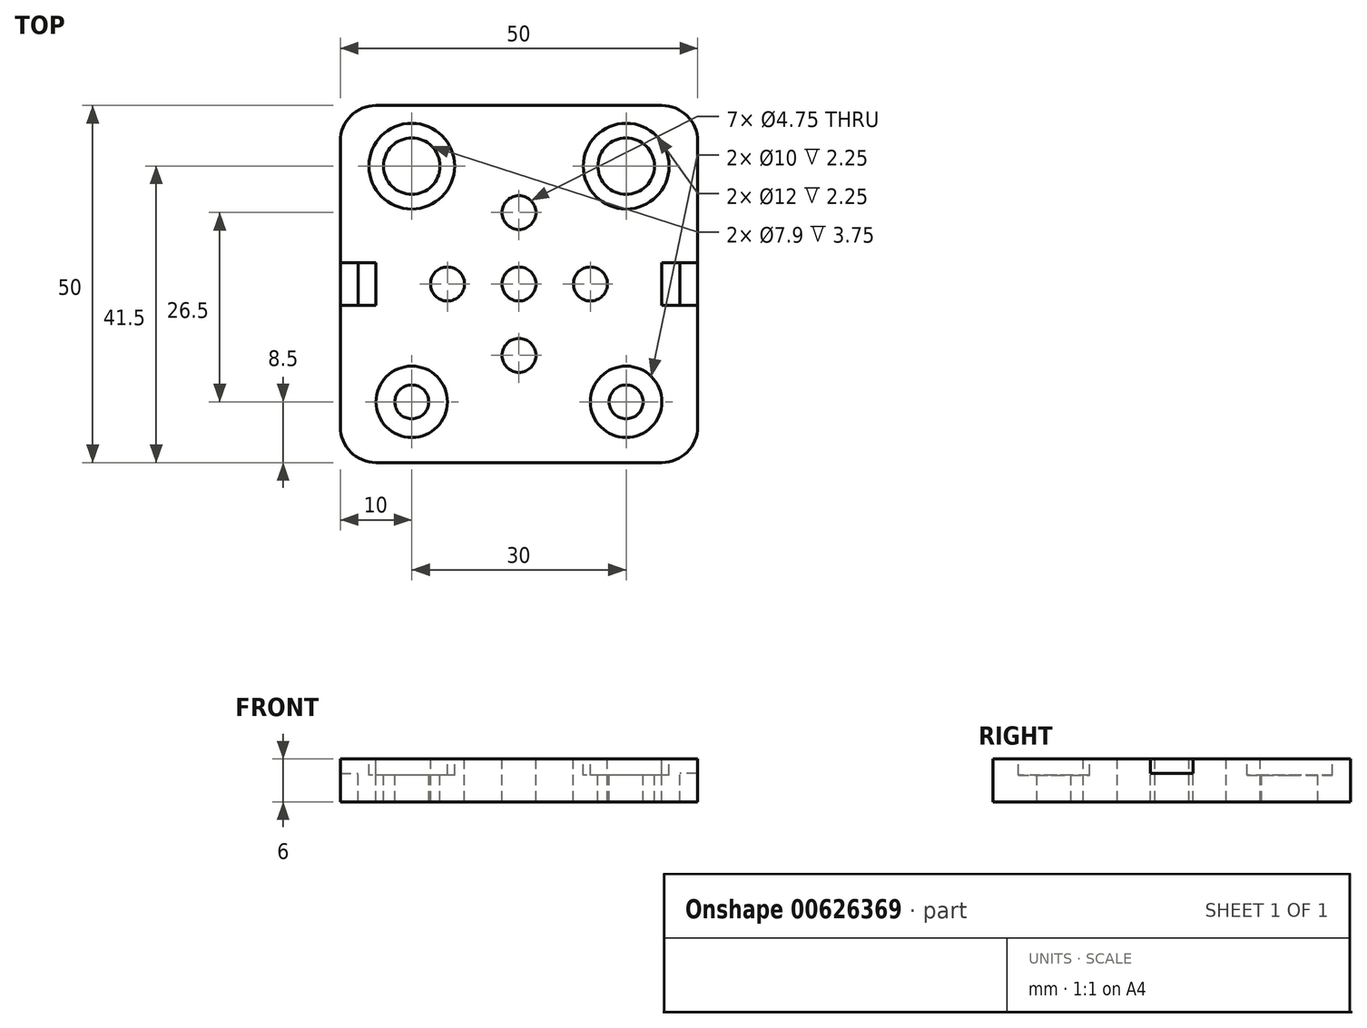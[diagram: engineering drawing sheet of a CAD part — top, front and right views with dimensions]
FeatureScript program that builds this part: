
annotation { "Feature Type Name" : "Feature", "Feature Type Description" : "" }
export const myFeature = defineFeature(function(context is Context, id is Id, definition is map)
    precondition{}
    {
        {
            var Q0;
            Q0=qCreatedBy(makeId("Top.planeOp"),FACE);
            var sketch = newSketch(context, id + "F0", { "sketchPlane" : qUnion([Q0])});
            skLineSegment(sketch, "E0.bottom", {"start": v(-20, -25) * mm, "end": v(20, -25) * mm});
            skLineSegment(sketch, "E0.top", {"start": v(-20, 25) * mm, "end": v(20, 25) * mm});
            skLineSegment(sketch, "E0.left", {"start": v(-25, -20) * mm, "end": v(-25, 20) * mm});
            skLineSegment(sketch, "E0.right", {"start": v(25, -20) * mm, "end": v(25, 20) * mm});
            skPoint(sketch, "E0.middle", {"position": v(0, 0) * mm});
            skPoint(sketch, "E1.visualSharp", {"position": v(-25, 25) * mm});
            skArc(sketch, "E1.filletArc", {"start": v(-20, 25) * mm, "mid": v(-23.54, 23.54) * mm, "end": v(-25, 20) * mm});
            skPoint(sketch, "E2.visualSharp", {"position": v(25, 25) * mm});
            skArc(sketch, "E2.filletArc", {"start": v(25, 20) * mm, "mid": v(23.54, 23.54) * mm, "end": v(20, 25) * mm});
            skPoint(sketch, "E3.visualSharp", {"position": v(25, -25) * mm});
            skArc(sketch, "E3.filletArc", {"start": v(20, -25) * mm, "mid": v(23.54, -23.54) * mm, "end": v(25, -20) * mm});
            skPoint(sketch, "E4.visualSharp", {"position": v(-25, -25) * mm});
            skArc(sketch, "E4.filletArc", {"start": v(-25, -20) * mm, "mid": v(-23.54, -23.54) * mm, "end": v(-20, -25) * mm});
            skSolve(sketch);
        }
        {
            var Q0;
            Q0=makeQuery(id+"F0.imprint","IMPRINT",FACE,{"disambiguationData":[TD([[makeQuery(id+"F0.imprint","IMPRINT",EDGE,{"derivedFrom":sQuery(id+"F0.wireOp",EDGE,"E0.bottom")}),1.0]])]});
            extrude(context, id + "F1", {"entities" : qUnion([Q0]), "depth" : 6 * mm, "offsetDistance" : 25 * mm});
        }
        {
            var Q0;
            Q0=makeQuery(id+"F1.opExtrude","CAP_FACE",FACE,{"disambiguationData":[OSD([sQuery(id+"F0.wireOp",EDGE,"E0.bottom"),sQuery(id+"F0.wireOp",EDGE,"E0.top"),sQuery(id+"F0.wireOp",EDGE,"E0.left"),sQuery(id+"F0.wireOp",EDGE,"E0.right"),sQuery(id+"F0.wireOp",EDGE,"E1.filletArc"),sQuery(id+"F0.wireOp",EDGE,"E2.filletArc"),sQuery(id+"F0.wireOp",EDGE,"E3.filletArc"),sQuery(id+"F0.wireOp",EDGE,"E4.filletArc")])],"isStart":false});
            var sketch = newSketch(context, id + "F2", { "sketchPlane" : qUnion([Q0])});
            skLineSegment(sketch, "E5.bottom", {"start": v(-25, 3) * mm, "end": v(-22.5, 3) * mm});
            skLineSegment(sketch, "E5.top", {"start": v(-25, -3) * mm, "end": v(-22.5, -3) * mm});
            skLineSegment(sketch, "E5.left", {"start": v(-25, 3) * mm, "end": v(-25, -3) * mm});
            skLineSegment(sketch, "E5.right", {"start": v(-22.5, 3) * mm, "end": v(-22.5, -3) * mm});
            skLineSegment(sketch, "E6.MirrorCS", {"start": v(25, 3) * mm, "end": v(22.5, 3) * mm});
            skLineSegment(sketch, "E7.MirrorCS", {"start": v(25, -3) * mm, "end": v(22.5, -3) * mm});
            skLineSegment(sketch, "E8.MirrorCS", {"start": v(25, 3) * mm, "end": v(25, -3) * mm});
            skLineSegment(sketch, "E9.MirrorCS", {"start": v(22.5, 3) * mm, "end": v(22.5, -3) * mm});
            skSolve(sketch);
        }
        {
            var Q0;
            Q0=qSketchRegion(id+"F2",true);
            extrude(context, id + "F3", {"entities" : qUnion([Q0]), "operationType" : NewBodyOperationType.REMOVE, "oppositeDirection" : true, "depth" : 2 * mm, "offsetDistance" : 25 * mm});
        }
        {
            var Q0;
            Q0=makeQuery(id+"F1.opExtrude","CAP_FACE",FACE,{"disambiguationData":[OSD([sQuery(id+"F0.wireOp",EDGE,"E0.bottom"),sQuery(id+"F0.wireOp",EDGE,"E0.top"),sQuery(id+"F0.wireOp",EDGE,"E0.left"),sQuery(id+"F0.wireOp",EDGE,"E0.right"),sQuery(id+"F0.wireOp",EDGE,"E1.filletArc"),sQuery(id+"F0.wireOp",EDGE,"E2.filletArc"),sQuery(id+"F0.wireOp",EDGE,"E3.filletArc"),sQuery(id+"F0.wireOp",EDGE,"E4.filletArc")])],"isStart":false});
            var sketch = newSketch(context, id + "F4", { "sketchPlane" : qUnion([Q0])});
            skLineSegment(sketch, "E10.bottom", {"start": v(-22.5, 3) * mm, "end": v(-20, 3) * mm});
            skLineSegment(sketch, "E10.top", {"start": v(-22.5, -3) * mm, "end": v(-20, -3) * mm});
            skLineSegment(sketch, "E10.left", {"start": v(-22.5, 3) * mm, "end": v(-22.5, -3) * mm});
            skLineSegment(sketch, "E10.right", {"start": v(-20, 3) * mm, "end": v(-20, -3) * mm});
            skLineSegment(sketch, "E11.MirrorCS", {"start": v(20, 3) * mm, "end": v(20, -3) * mm});
            skLineSegment(sketch, "E12.MirrorCS", {"start": v(22.5, 3) * mm, "end": v(22.5, -3) * mm});
            skLineSegment(sketch, "E13.MirrorCS", {"start": v(22.5, -3) * mm, "end": v(20, -3) * mm});
            skLineSegment(sketch, "E14.MirrorCS", {"start": v(22.5, 3) * mm, "end": v(20, 3) * mm});
            skSolve(sketch);
        }
        {
            var Q0;
            Q0=qSketchRegion(id+"F4",true);
            extrude(context, id + "F5", {"entities" : qUnion([Q0]), "operationType" : NewBodyOperationType.REMOVE, "oppositeDirection" : true, "depth" : 25 * mm, "offsetDistance" : 25 * mm});
        }
        {
            var Q0;
            Q0=makeQuery(id+"F1.opExtrude","CAP_FACE",FACE,{"disambiguationData":[OSD([sQuery(id+"F0.wireOp",EDGE,"E0.bottom"),sQuery(id+"F0.wireOp",EDGE,"E0.top"),sQuery(id+"F0.wireOp",EDGE,"E0.left"),sQuery(id+"F0.wireOp",EDGE,"E0.right"),sQuery(id+"F0.wireOp",EDGE,"E1.filletArc"),sQuery(id+"F0.wireOp",EDGE,"E2.filletArc"),sQuery(id+"F0.wireOp",EDGE,"E3.filletArc"),sQuery(id+"F0.wireOp",EDGE,"E4.filletArc")])],"isStart":false});
            var sketch = newSketch(context, id + "F6", { "sketchPlane" : qUnion([Q0])});
            skCircle(sketch, "E15", {"center": v(0, 0) * mm, "radius": 2.38 * mm});
            skCircle(sketch, "E16", {"center": v(-10, 0) * mm, "radius": 2.38 * mm});
            skCircle(sketch, "E17.1.0", {"center": v(0, -10) * mm, "radius": 2.38 * mm});
            skCircle(sketch, "E17.2.0", {"center": v(10, 0) * mm, "radius": 2.38 * mm});
            skCircle(sketch, "E17.3.0", {"center": v(0, 10) * mm, "radius": 2.38 * mm});
            skSolve(sketch);
        }
        {
            var Q0;
            Q0=qSketchRegion(id+"F6",true);
            extrude(context, id + "F7", {"entities" : qUnion([Q0]), "operationType" : NewBodyOperationType.REMOVE, "oppositeDirection" : true, "depth" : 25 * mm, "offsetDistance" : 25 * mm});
        }
        {
            var Q0;
            Q0=makeQuery(id+"F1.opExtrude","CAP_FACE",FACE,{"disambiguationData":[OSD([sQuery(id+"F0.wireOp",EDGE,"E0.bottom"),sQuery(id+"F0.wireOp",EDGE,"E0.top"),sQuery(id+"F0.wireOp",EDGE,"E0.left"),sQuery(id+"F0.wireOp",EDGE,"E0.right"),sQuery(id+"F0.wireOp",EDGE,"E1.filletArc"),sQuery(id+"F0.wireOp",EDGE,"E2.filletArc"),sQuery(id+"F0.wireOp",EDGE,"E3.filletArc"),sQuery(id+"F0.wireOp",EDGE,"E4.filletArc")])],"isStart":false});
            var sketch = newSketch(context, id + "F8", { "sketchPlane" : qUnion([Q0])});
            skCircle(sketch, "E18", {"center": v(-15, -16.5) * mm, "radius": 2.38 * mm});
            skCircle(sketch, "E19.MirrorC", {"center": v(15, -16.5) * mm, "radius": 2.38 * mm});
            skCircle(sketch, "E20.MirrorC", {"center": v(-15, 16.5) * mm, "radius": 2.38 * mm});
            skCircle(sketch, "E21.MirrorC", {"center": v(15, 16.5) * mm, "radius": 2.38 * mm});
            skSolve(sketch);
        }
        {
            var Q0;
            Q0=qSketchRegion(id+"F8",true);
            extrude(context, id + "F9", {"entities" : qUnion([Q0]), "operationType" : NewBodyOperationType.REMOVE, "oppositeDirection" : true, "depth" : 25 * mm, "offsetDistance" : 25 * mm});
        }
        {
            var Q0;
            Q0=makeQuery(id+"F1.opExtrude","CAP_FACE",FACE,{"disambiguationData":[OSD([sQuery(id+"F0.wireOp",EDGE,"E0.bottom"),sQuery(id+"F0.wireOp",EDGE,"E0.top"),sQuery(id+"F0.wireOp",EDGE,"E0.left"),sQuery(id+"F0.wireOp",EDGE,"E0.right"),sQuery(id+"F0.wireOp",EDGE,"E1.filletArc"),sQuery(id+"F0.wireOp",EDGE,"E2.filletArc"),sQuery(id+"F0.wireOp",EDGE,"E3.filletArc"),sQuery(id+"F0.wireOp",EDGE,"E4.filletArc")])],"isStart":false});
            var sketch = newSketch(context, id + "F10", { "sketchPlane" : qUnion([Q0])});
            skCircle(sketch, "E22", {"center": v(-15, 16.5) * mm, "radius": 6 * mm});
            skCircle(sketch, "E23", {"center": v(15, 16.5) * mm, "radius": 6 * mm});
            skCircle(sketch, "E24", {"center": v(-15, -16.5) * mm, "radius": 5 * mm});
            skCircle(sketch, "E25", {"center": v(15, -16.5) * mm, "radius": 5 * mm});
            skSolve(sketch);
        }
        {
            var Q0;
            Q0=qSketchRegion(id+"F10",true);
            extrude(context, id + "F11", {"entities" : qUnion([Q0]), "operationType" : NewBodyOperationType.REMOVE, "oppositeDirection" : true, "depth" : 2.25 * mm, "offsetDistance" : 25 * mm});
        }
        {
            var Q0;
            Q0=makeQuery(id+"F11.boolean.opBoolean","COPY",FACE,{"derivedFrom":makeQuery(id+"F11.opExtrude","CAP_FACE",FACE,{"disambiguationData":[OSD([sQuery(id+"F10.wireOp",EDGE,"E22")])],"isStart":false})});
            var sketch = newSketch(context, id + "F12", { "sketchPlane" : qUnion([Q0])});
            skCircle(sketch, "E26", {"center": v(-15, 16.5) * mm, "radius": 3.95 * mm});
            skCircle(sketch, "E27.MirrorC", {"center": v(15, 16.5) * mm, "radius": 3.95 * mm});
            skSolve(sketch);
        }
        {
            var Q0;
            Q0=qSketchRegion(id+"F12",true);
            extrude(context, id + "F13", {"entities" : qUnion([Q0]), "operationType" : NewBodyOperationType.REMOVE, "oppositeDirection" : true, "depth" : 25 * mm, "offsetDistance" : 25 * mm});
        }
    });
